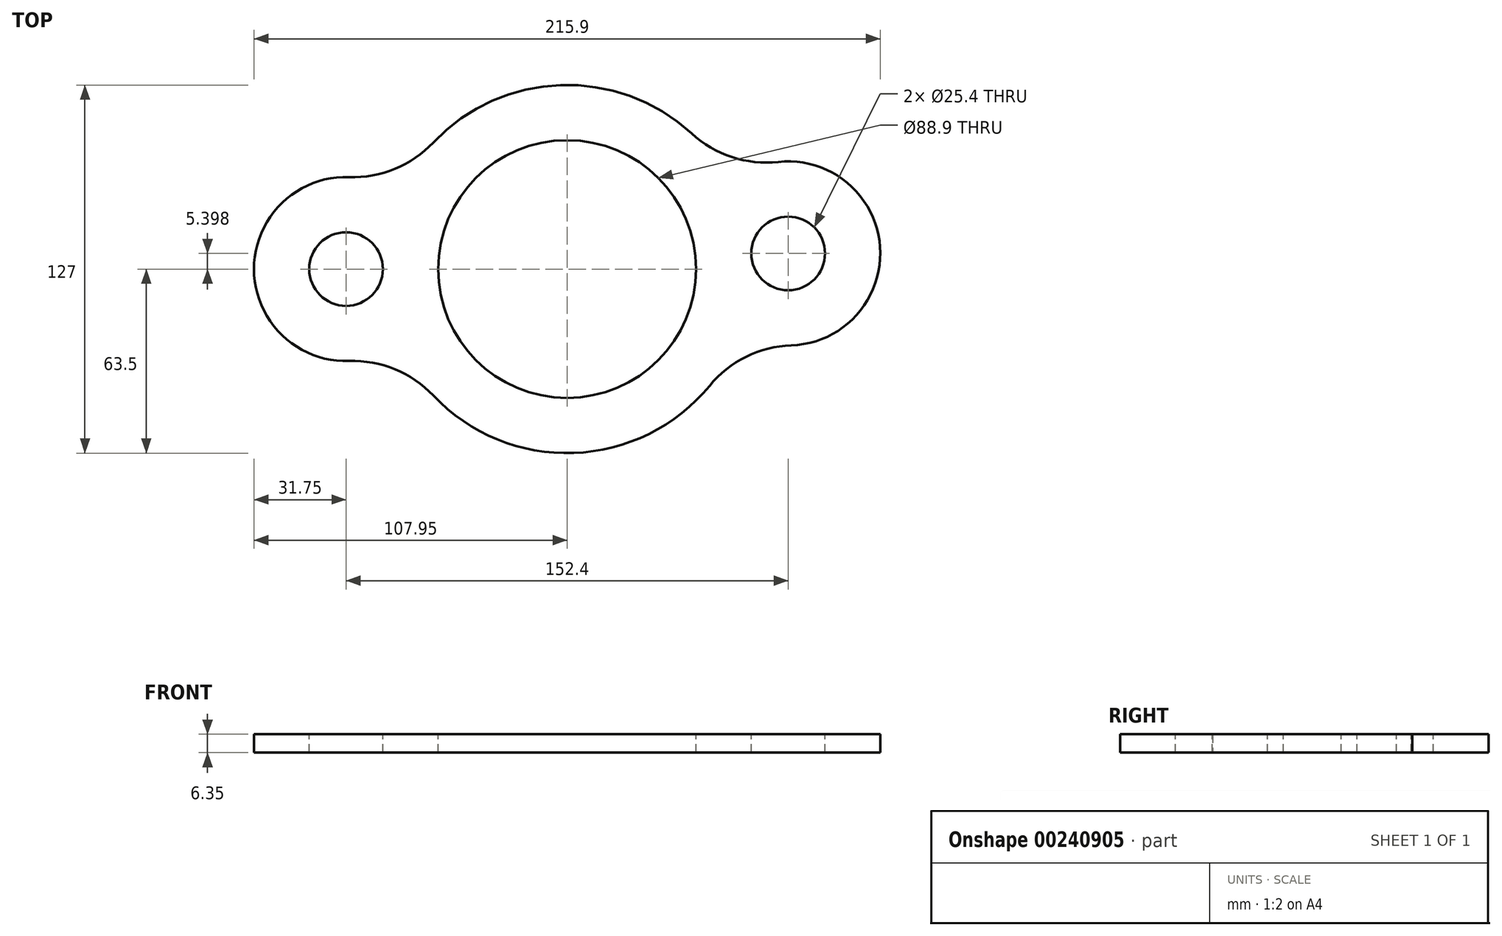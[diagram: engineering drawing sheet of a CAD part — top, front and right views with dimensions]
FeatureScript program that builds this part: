
annotation { "Feature Type Name" : "Feature", "Feature Type Description" : "" }
export const myFeature = defineFeature(function(context is Context, id is Id, definition is map)
    precondition{}
    {
        {
            var Q0;
            Q0=qCreatedBy(makeId("Top.planeOp"),FACE);
            var sketch = newSketch(context, id + "F0", { "sketchPlane" : qUnion([Q0])});
            skCircle(sketch, "E0", {"center": v(0, 0) * mm, "radius": 44.45 * mm});
            skCircle(sketch, "E1", {"center": v(0, 0) * mm, "radius": 63.5 * mm});
            skSolve(sketch);
        }
        {
            var Q0;
            Q0=makeQuery(id+"F0.imprint","IMPRINT",FACE,{"disambiguationData":[TD([[makeQuery(id+"F0.imprint","IMPRINT",EDGE,{"derivedFrom":sQuery(id+"F0.wireOp",EDGE,"E0")}),-1.0]])]});
            extrude(context, id + "F1", {"entities" : qUnion([Q0]), "oppositeDirection" : true, "depth" : 6.35 * mm});
        }
        {
            var Q0;
            Q0=qCreatedBy(makeId("Top.planeOp"),FACE);
            var sketch = newSketch(context, id + "F2", { "sketchPlane" : qUnion([Q0])});
            skCircle(sketch, "E2", {"center": v(-76.2, 0) * mm, "radius": 12.7 * mm});
            skCircle(sketch, "E3", {"center": v(-76.2, 0) * mm, "radius": 31.75 * mm});
            skSolve(sketch);
        }
        {
            var Q0;
            Q0=makeQuery(id+"F2.imprint","IMPRINT",FACE,{"disambiguationData":[TD([[makeQuery(id+"F2.imprint","IMPRINT",EDGE,{"derivedFrom":sQuery(id+"F2.wireOp",EDGE,"E2")}),-1.0]])]});
            extrude(context, id + "F3", {"entities" : qUnion([Q0]), "oppositeDirection" : true, "depth" : 6.35 * mm});
        }
        {
            var Q0;
            Q0=qCreatedBy(makeId("Top.planeOp"),FACE);
            var sketch = newSketch(context, id + "F4", { "sketchPlane" : qUnion([Q0])});
            skCircle(sketch, "E4", {"center": v(76.2, 5.4) * mm, "radius": 12.7 * mm});
            skCircle(sketch, "E5", {"center": v(76.2, 5.4) * mm, "radius": 31.75 * mm});
            skSolve(sketch);
        }
        {
            var Q0;
            Q0=makeQuery(id+"F4.imprint","IMPRINT",FACE,{"disambiguationData":[TD([[makeQuery(id+"F4.imprint","IMPRINT",EDGE,{"derivedFrom":sQuery(id+"F4.wireOp",EDGE,"E4")}),-1.0]])]});
            extrude(context, id + "F5", {"entities" : qUnion([Q0]), "oppositeDirection" : true, "depth" : 6.35 * mm});
        }
        {
            var Q0;
            Q0=makeQuery(id+"F5.opExtrude","SWEPT_BODY",BODY,{"disambiguationData":[OSD([sQuery(id+"F4.wireOp",EDGE,"E4"),sQuery(id+"F4.wireOp",EDGE,"E5")])]});
            var Q1;
            Q1=makeQuery(id+"F1.opExtrude","SWEPT_BODY",BODY,{"disambiguationData":[OSD([sQuery(id+"F0.wireOp",EDGE,"E0"),sQuery(id+"F0.wireOp",EDGE,"E1")])]});
            booleanBodies(context, id + "F6", {"operationType" : BooleanOperationType.UNION, "tools" : qUnion([Q0, Q1])});
        }
        {
            var Q0;
            Q0=makeQuery(id+"F5.opExtrude","SWEPT_BODY",BODY,{"disambiguationData":[OSD([sQuery(id+"F4.wireOp",EDGE,"E4"),sQuery(id+"F4.wireOp",EDGE,"E5")])]});
            var Q1;
            Q1=makeQuery(id+"F3.opExtrude","SWEPT_BODY",BODY,{"disambiguationData":[OSD([sQuery(id+"F2.wireOp",EDGE,"E2"),sQuery(id+"F2.wireOp",EDGE,"E3")])]});
            booleanBodies(context, id + "F7", {"operationType" : BooleanOperationType.UNION, "tools" : qUnion([Q0, Q1])});
        }
        {
            var Q0;
            Q0=makeQuery(id+"F7.opBoolean","INTERSECT",EDGE,{"disambiguationData":[OD(1.0)],"derivedFrom":[makeQuery(id+"F3.opExtrude","SWEPT_FACE",FACE,{"disambiguationData":[OSD([sQuery(id+"F2.wireOp",EDGE,"E3")])]}),makeQuery(id+"F1.opExtrude","SWEPT_FACE",FACE,{"disambiguationData":[OSD([sQuery(id+"F0.wireOp",EDGE,"E1")])]})]});
            fillet(context, id + "F8", {"entities" : qUnion([Q0]), "radius" : 38.1 * mm, "tangentPropagation" : true, "allowEdgeOverflow" : false});
        }
        {
            var Q0;
            Q0=makeQuery(id+"F6.opBoolean","INTERSECT",EDGE,{"disambiguationData":[OD(1.0)],"derivedFrom":[makeQuery(id+"F1.opExtrude","SWEPT_FACE",FACE,{"disambiguationData":[OSD([sQuery(id+"F0.wireOp",EDGE,"E1")])]}),makeQuery(id+"F5.opExtrude","SWEPT_FACE",FACE,{"disambiguationData":[OSD([sQuery(id+"F4.wireOp",EDGE,"E5")])]})]});
            fillet(context, id + "F9", {"entities" : qUnion([Q0]), "radius" : 38.1 * mm, "tangentPropagation" : true, "allowEdgeOverflow" : false});
        }
        {
            var Q0;
            Q0=makeQuery(id+"F6.opBoolean","INTERSECT",EDGE,{"disambiguationData":[OD(0.0)],"derivedFrom":[makeQuery(id+"F1.opExtrude","SWEPT_FACE",FACE,{"disambiguationData":[OSD([sQuery(id+"F0.wireOp",EDGE,"E1")])]}),makeQuery(id+"F5.opExtrude","SWEPT_FACE",FACE,{"disambiguationData":[OSD([sQuery(id+"F4.wireOp",EDGE,"E5")])]})]});
            fillet(context, id + "F10", {"entities" : qUnion([Q0]), "radius" : 38.1 * mm, "tangentPropagation" : true, "allowEdgeOverflow" : false});
        }
        {
            var Q0;
            Q0=makeQuery(id+"F7.opBoolean","INTERSECT",EDGE,{"disambiguationData":[OD(0.0)],"derivedFrom":[makeQuery(id+"F3.opExtrude","SWEPT_FACE",FACE,{"disambiguationData":[OSD([sQuery(id+"F2.wireOp",EDGE,"E3")])]}),makeQuery(id+"F1.opExtrude","SWEPT_FACE",FACE,{"disambiguationData":[OSD([sQuery(id+"F0.wireOp",EDGE,"E1")])]})]});
            fillet(context, id + "F11", {"entities" : qUnion([Q0]), "radius" : 38.1 * mm, "tangentPropagation" : true, "allowEdgeOverflow" : false});
        }
    });
